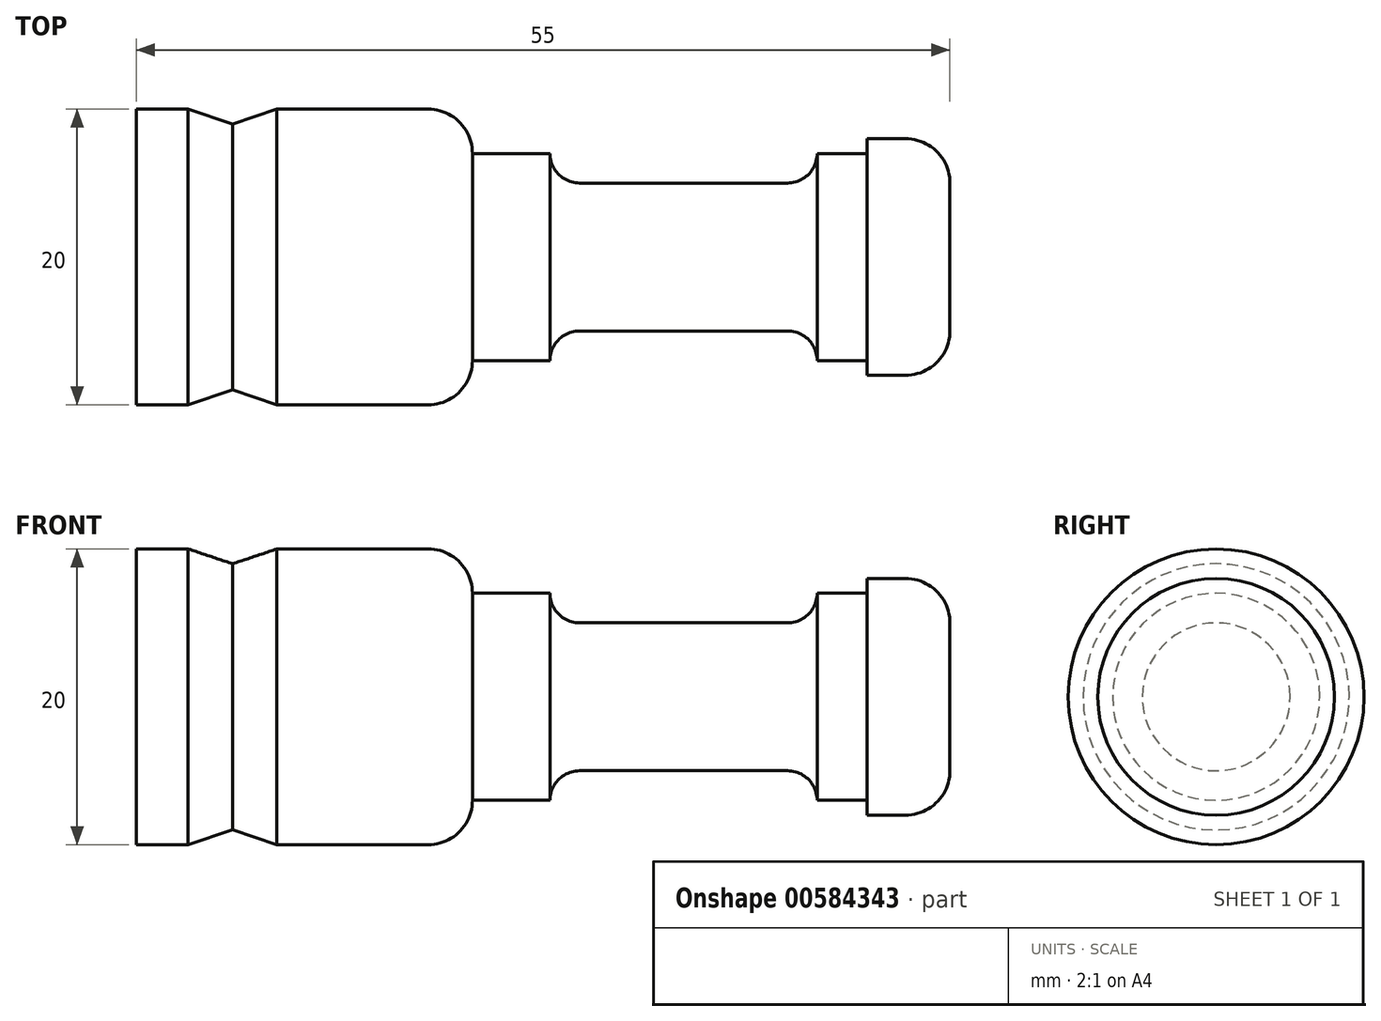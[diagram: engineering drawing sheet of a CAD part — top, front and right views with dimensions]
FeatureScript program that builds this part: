
annotation { "Feature Type Name" : "Feature", "Feature Type Description" : "" }
export const myFeature = defineFeature(function(context is Context, id is Id, definition is map)
    precondition{}
    {
        {
            var Q0;
            Q0=qCreatedBy(makeId("Front.planeOp"),FACE);
            var sketch = newSketch(context, id + "F0", { "sketchPlane" : qUnion([Q0])});
            skLineSegment(sketch, "E0", {"start": v(-41.57, -16.63) * mm, "end": v(40.6, -16.63) * mm, "construction": true});
            skLineSegment(sketch, "E1", {"start": v(-27.96, -16.63) * mm, "end": v(-27.96, -26.63) * mm});
            skLineSegment(sketch, "E2", {"start": v(-27.96, -26.63) * mm, "end": v(-24.46, -26.63) * mm});
            skLineSegment(sketch, "E3", {"start": v(-24.46, -26.63) * mm, "end": v(-21.46, -25.63) * mm});
            skLineSegment(sketch, "E4", {"start": v(-21.46, -25.63) * mm, "end": v(-18.46, -26.63) * mm});
            skLineSegment(sketch, "E5", {"start": v(-18.46, -26.63) * mm, "end": v(-8.24, -26.63) * mm});
            skLineSegment(sketch, "E6", {"start": v(-5.24, -23.63) * mm, "end": v(-5.24, -23.63) * mm});
            skLineSegment(sketch, "E7", {"start": v(-5.24, -23.63) * mm, "end": v(0, -23.63) * mm});
            skLineSegment(sketch, "E8", {"start": v(0, -23.63) * mm, "end": v(0, -23.63) * mm});
            skLineSegment(sketch, "E9", {"start": v(2, -21.63) * mm, "end": v(16.06, -21.63) * mm});
            skLineSegment(sketch, "E10", {"start": v(18.06, -23.63) * mm, "end": v(18.06, -23.63) * mm});
            skLineSegment(sketch, "E11", {"start": v(18.06, -23.63) * mm, "end": v(21.45, -23.63) * mm});
            skLineSegment(sketch, "E12", {"start": v(21.45, -23.63) * mm, "end": v(21.45, -24.63) * mm});
            skLineSegment(sketch, "E13", {"start": v(21.45, -24.63) * mm, "end": v(24.04, -24.63) * mm});
            skLineSegment(sketch, "E14", {"start": v(27.04, -21.63) * mm, "end": v(27.04, -16.63) * mm});
            skLineSegment(sketch, "E15", {"start": v(27.04, -16.63) * mm, "end": v(-27.96, -16.63) * mm});
            skPoint(sketch, "E16.visualSharp", {"position": v(-5.24, -26.63) * mm});
            skArc(sketch, "E16.filletArc", {"start": v(-8.24, -26.63) * mm, "mid": v(-6.12, -25.75) * mm, "end": v(-5.24, -23.63) * mm});
            skPoint(sketch, "E17.visualSharp", {"position": v(0, -21.63) * mm});
            skArc(sketch, "E17.filletArc", {"start": v(2, -21.63) * mm, "mid": v(0.59, -22.21) * mm, "end": v(0, -23.63) * mm});
            skPoint(sketch, "E18.visualSharp", {"position": v(18.06, -21.63) * mm});
            skArc(sketch, "E18.filletArc", {"start": v(18.06, -23.63) * mm, "mid": v(17.48, -22.21) * mm, "end": v(16.06, -21.63) * mm});
            skPoint(sketch, "E19.visualSharp", {"position": v(27.04, -24.63) * mm});
            skArc(sketch, "E19.filletArc", {"start": v(24.04, -24.63) * mm, "mid": v(26.16, -23.75) * mm, "end": v(27.04, -21.63) * mm});
            skSolve(sketch);
        }
        {
            var Q0;
            Q0=makeQuery(id+"F0.imprint","IMPRINT",FACE,{"disambiguationData":[TD([[makeQuery(id+"F0.imprint","IMPRINT",EDGE,{"derivedFrom":sQuery(id+"F0.wireOp",EDGE,"E1")}),1.0]])]});
            var Q1;
            Q1=sQuery(id+"F0.wireOp",EDGE,"E0");
            revolve(context, id + "F1", {"entities" : qUnion([Q0]), "axis" : qUnion([Q1]), "revolveType" : RevolveType.FULL});
        }
    });
